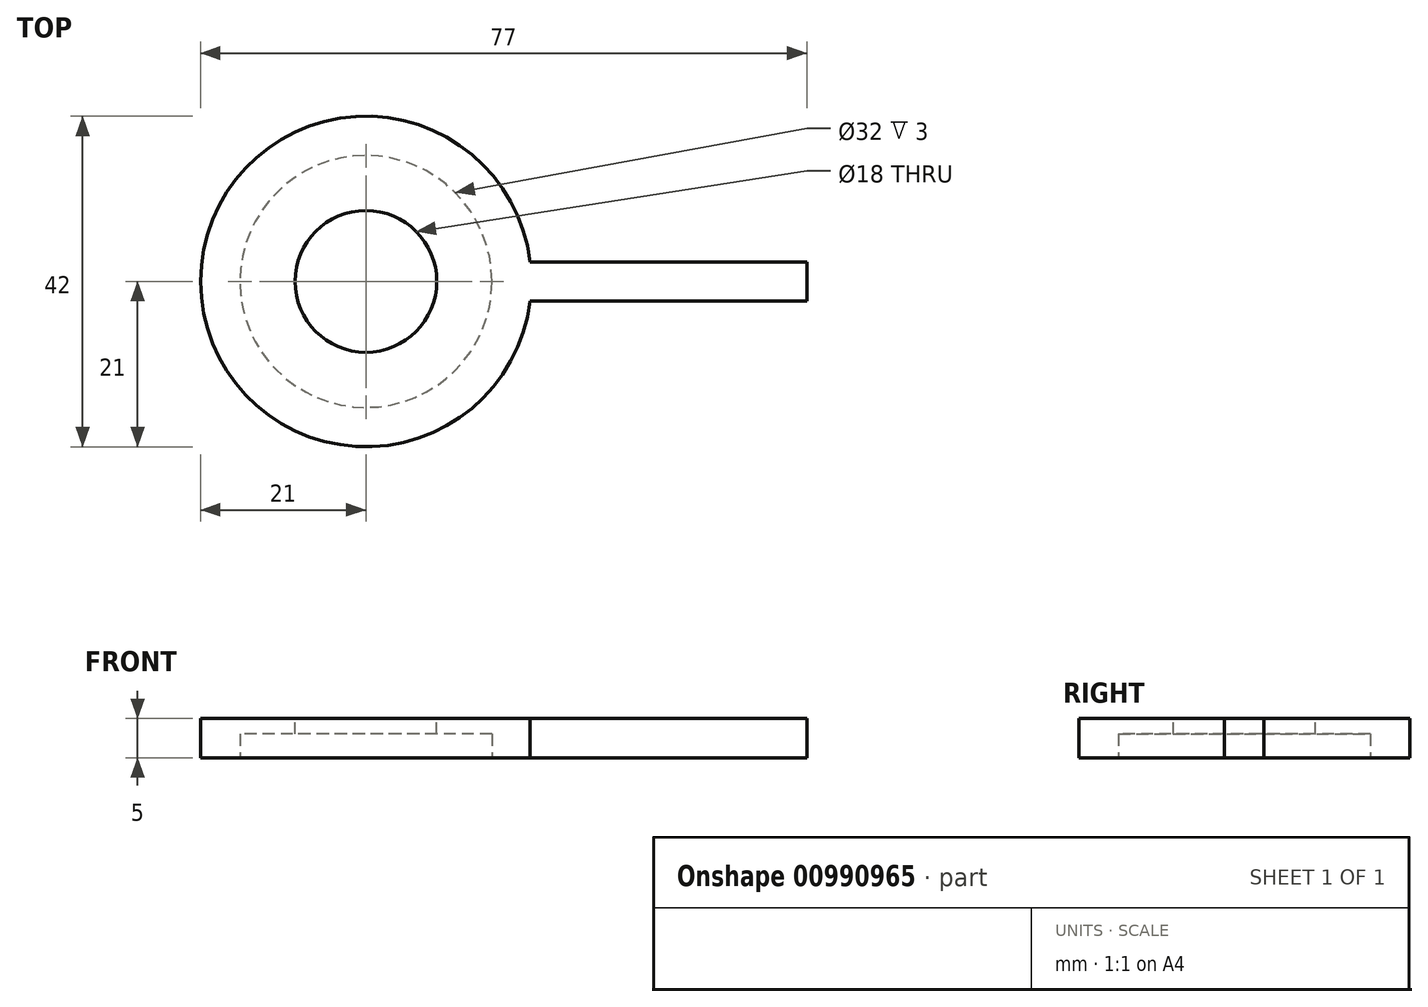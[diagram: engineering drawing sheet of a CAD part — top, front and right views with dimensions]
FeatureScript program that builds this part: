
annotation { "Feature Type Name" : "Feature", "Feature Type Description" : "" }
export const myFeature = defineFeature(function(context is Context, id is Id, definition is map)
    precondition{}
    {
        {
            var Q0;
            Q0=qCreatedBy(makeId("Top.planeOp"),FACE);
            var sketch = newSketch(context, id + "F0", { "sketchPlane" : qUnion([Q0])});
            skCircle(sketch, "E0", {"center": v(0, 0) * mm, "radius": 16 * mm});
            skCircle(sketch, "E1", {"center": v(0, 0) * mm, "radius": 21 * mm});
            skLineSegment(sketch, "E2", {"start": v(0, 0) * mm, "end": v(90.45, 0) * mm, "construction": true});
            skLineSegment(sketch, "E3", {"start": v(56, 0) * mm, "end": v(56, 2.5) * mm});
            skLineSegment(sketch, "E4", {"start": v(56, 2.5) * mm, "end": v(20.85, 2.5) * mm});
            skPoint(sketch, "E5", {"position": v(21, 0) * mm});
            skLineSegment(sketch, "E6.MirrorCS", {"start": v(56, -2.5) * mm, "end": v(20.85, -2.5) * mm});
            skLineSegment(sketch, "E7.MirrorCS", {"start": v(56, 0) * mm, "end": v(56, -2.5) * mm});
            skSolve(sketch);
        }
        {
            var Q0;
            Q0=makeQuery(id+"F0.imprint","IMPRINT",FACE,{"disambiguationData":[TD([[makeQuery(id+"F0.imprint","IMPRINT",EDGE,{"derivedFrom":sQuery(id+"F0.wireOp",EDGE,"E0")}),-1.0]])]});
            var Q1;
            Q1=makeQuery(id+"F0.imprint","IMPRINT",FACE,{"disambiguationData":[TD([[makeQuery(id+"F0.imprint","IMPRINT",EDGE,{"derivedFrom":sQuery(id+"F0.wireOp",EDGE,"E3")}),1.0]])]});
            var Q2;
            Q2=makeQuery(id+"F0.imprint","IMPRINT",FACE,{"disambiguationData":[TD([[makeQuery(id+"F0.imprint","IMPRINT",EDGE,{"derivedFrom":sQuery(id+"F0.wireOp",EDGE,"E0")}),1.0]])]});
            extrude(context, id + "F1", {"entities" : qUnion([Q0, Q1, Q2]), "depth" : 5 * mm, "offsetDistance" : 25 * mm});
        }
        {
            var Q0;
            Q0=makeQuery(id+"F0.imprint","IMPRINT",FACE,{"disambiguationData":[TD([[makeQuery(id+"F0.imprint","IMPRINT",EDGE,{"derivedFrom":sQuery(id+"F0.wireOp",EDGE,"E0")}),1.0]])]});
            extrude(context, id + "F2", {"entities" : qUnion([Q0]), "operationType" : NewBodyOperationType.REMOVE, "depth" : 3 * mm, "offsetDistance" : 25 * mm});
        }
        {
            var Q0;
            Q0=makeQuery(id+"F1.opExtrude","CAP_FACE",FACE,{"disambiguationData":[OSD([sQuery(id+"F0.wireOp",EDGE,"E1"),sQuery(id+"F0.wireOp",EDGE,"E3"),sQuery(id+"F0.wireOp",EDGE,"E4"),sQuery(id+"F0.wireOp",EDGE,"E6.MirrorCS"),sQuery(id+"F0.wireOp",EDGE,"E7.MirrorCS")])],"isStart":false});
            var sketch = newSketch(context, id + "F3", { "sketchPlane" : qUnion([Q0])});
            skCircle(sketch, "E8", {"center": v(0, 0) * mm, "radius": 9 * mm});
            skSolve(sketch);
        }
        {
            var Q0;
            Q0=makeQuery(id+"F3.imprint","IMPRINT",FACE,{"disambiguationData":[TD([[makeQuery(id+"F3.imprint","IMPRINT",EDGE,{"derivedFrom":sQuery(id+"F3.wireOp",EDGE,"E8")}),1.0]])]});
            extrude(context, id + "F4", {"entities" : qUnion([Q0]), "operationType" : NewBodyOperationType.REMOVE, "endBound" : BoundingType.THROUGH_ALL, "oppositeDirection" : true, "depth" : 2 * mm, "offsetDistance" : 25 * mm});
        }
    });
